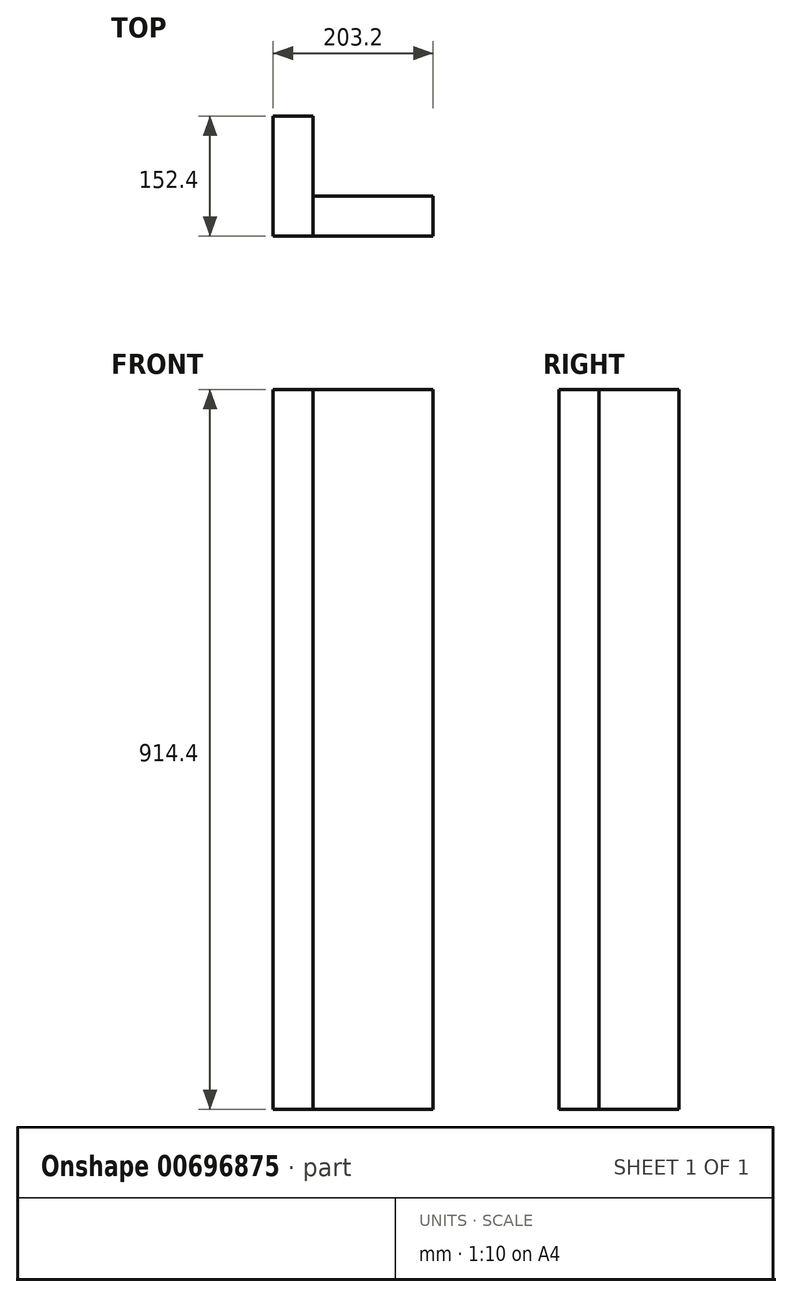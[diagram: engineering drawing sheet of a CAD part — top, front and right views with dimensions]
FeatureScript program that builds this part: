
annotation { "Feature Type Name" : "Feature", "Feature Type Description" : "" }
export const myFeature = defineFeature(function(context is Context, id is Id, definition is map)
    precondition{}
    {
        {
            var Q0;
            Q0=qCreatedBy(makeId("Top.planeOp"),FACE);
            var sketch = newSketch(context, id + "F0", { "sketchPlane" : qUnion([Q0])});
            skLineSegment(sketch, "E0.bottom", {"start": v(0, 0) * mm, "end": v(152.4, 0) * mm});
            skLineSegment(sketch, "E0.top", {"start": v(0, -50.8) * mm, "end": v(152.4, -50.8) * mm});
            skLineSegment(sketch, "E0.left", {"start": v(0, 0) * mm, "end": v(0, -50.8) * mm});
            skLineSegment(sketch, "E0.right", {"start": v(152.4, 0) * mm, "end": v(152.4, -50.8) * mm});
            skLineSegment(sketch, "E1.bottom", {"start": v(0, -50.8) * mm, "end": v(-50.8, -50.8) * mm});
            skLineSegment(sketch, "E1.top", {"start": v(0, 101.6) * mm, "end": v(-50.8, 101.6) * mm});
            skLineSegment(sketch, "E1.left", {"start": v(0, -50.8) * mm, "end": v(0, 101.6) * mm});
            skLineSegment(sketch, "E1.right", {"start": v(-50.8, -50.8) * mm, "end": v(-50.8, 101.6) * mm});
            skSolve(sketch);
        }
        {
            var Q0;
            {var subQ0=sQuery(id+"F0.wireOp",EDGE,"E0.bottom");Q0=makeQuery(id+"F0.imprint","IMPRINT",FACE,{"disambiguationData":[TD([[makeQuery(id+"F0.imprint","IMPRINT",EDGE,{"derivedFrom":subQ0}),-1.0]])]});}
            extrude(context, id + "F1", {"entities" : qUnion([Q0]), "oppositeDirection" : true, "depth" : 914.4 * mm, "offsetDistance" : 25.4 * mm});
        }
        {
            var Q0;
            {var subQ3=sQuery(id+"F0.wireOp",EDGE,"E1.bottom");Q0=makeQuery(id+"F0.imprint","IMPRINT",FACE,{"disambiguationData":[TD([[makeQuery(id+"F0.imprint","IMPRINT",EDGE,{"derivedFrom":subQ3}),-1.0]])]});}
            extrude(context, id + "F2", {"entities" : qUnion([Q0]), "oppositeDirection" : true, "depth" : 914.4 * mm, "offsetDistance" : 25.4 * mm});
        }
    });
